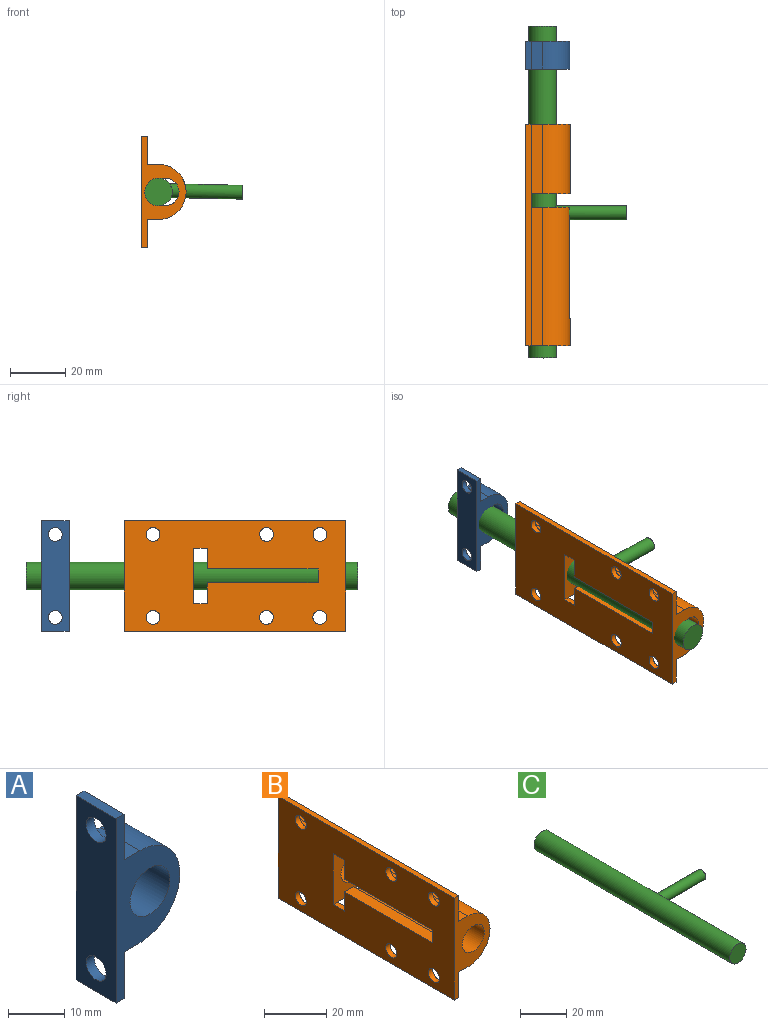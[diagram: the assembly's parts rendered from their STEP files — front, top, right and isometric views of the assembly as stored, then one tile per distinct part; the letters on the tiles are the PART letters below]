
ASSEMBLY  parts=3 mates=2
PART A: 13 faces, bbox 16x10x40 mm
  f0: plane 40x16mm, normal (0,-1,0), area 238.5mm2, adj f1,f3,f4,f5,f6,f7,f8,f9
  f1: plane 10x4mm, normal (0,0,-1), area 40mm2, adj f0,f2,f6,f9
  f2: plane 40x16mm, normal (0,1,0), area 238.5mm2, adj f1,f3,f4,f5,f6,f7,f8,f9
  f3: plane 10x4mm, normal (0,0,1), area 40mm2, adj f0,f2,f8,f9
  f4: plane 10x2mm, normal (0,0,-1), area 20mm2, adj f0,f2,f5,f6
  f5: plane 40x10mm, normal (-1,0,0), area 360.7mm2, adj f0,f2,f4,f7,f11,f12
  f6: plane 10.06x10mm, normal (1,0,0), area 81mm2, adj f0,f1,f2,f4,f12
  f7: plane 10x2mm, normal (0,0,1), area 20mm2, adj f0,f2,f5,f8
  f8: plane 10x9.94mm, normal (1,0,0), area 79.7mm2, adj f0,f2,f3,f7,f11
  f9: cylinder r=10mm len=20mm, axis (0,1,0), area 314.2mm2, adj f0,f1,f2,f3
  f10: cylinder r=5mm len=10mm, axis (0,1,0), area 314.2mm2, adj f0,f2
  f11: cylinder r=2.5mm len=5mm, axis (1,0,0), area 31.4mm2, adj f5,f8
  f12: cylinder r=2.5mm len=5mm, axis (1,0,0), area 31.4mm2, adj f5,f6
PART B: 32 faces, bbox 16.1x80x40 mm
  f0: plane 5x2mm, normal (0,0,1), area 10mm2, adj f2,f12,f13,f19
  f1: plane 5x2mm, normal (0,0,-1), area 10mm2, adj f12,f15,f18,f19
  f2: plane 15.78x7.5mm, normal (0,1,0), area 84.2mm2, adj f0,f3,f12,f16,f17,f22,f24
  f3: plane 50x4.1mm, normal (0,0,-1), area 205mm2, adj f2,f7,f13,f16
  f4: plane 50x4.1mm, normal (0,0,1), area 205mm2, adj f7,f15,f16,f18
  f5: cylinder r=10mm len=25mm, axis (0,-1,0), area 785.4mm2, adj f8,f9,f10,f19
  f6: cylinder r=5mm len=25mm, axis (0,-1,0), area 785.4mm2, adj f9,f19
  f7: plane 40x16.1mm, normal (0,-1,0), area 240.5mm2, adj f3,f4,f11,f12,f13,f14,f15,f16
  f8: plane 25x4.1mm, normal (0,0,-1), area 102.5mm2, adj f5,f9,f13,f19
  f9: plane 40x16.1mm, normal (0,1,0), area 240.5mm2, adj f5,f6,f8,f10,f11,f12,f13,f14
  f10: plane 25x4.1mm, normal (0,0,1), area 102.5mm2, adj f5,f9,f15,f19
  f11: plane 80x2mm, normal (0,0,-1), area 160mm2, adj f7,f9,f12,f13
  f12: plane 80x40mm, normal (-1,0,0), area 2782.2mm2, adj f0,f1,f2,f7,f9,f11,f14,f18
  f13: plane 80x10mm, normal (1,0,0), area 741.1mm2, adj f0,f3,f7,f8,f9,f11,f29,f30
  f14: plane 80x2mm, normal (0,0,1), area 160mm2, adj f7,f9,f12,f15
  f15: plane 80x10mm, normal (1,0,0), area 741.1mm2, adj f1,f4,f7,f9,f10,f14,f26,f27
  f16: cylinder r=10mm len=50mm, axis (0,-1,0), area 1368.7mm2, adj f2,f3,f4,f7,f18,f23,f24,f25
  f17: cylinder r=5mm len=50mm, axis (0,-1,0), area 1151.9mm2, adj f2,f7,f18,f20,f21,f22,f23,f24
  f18: plane 15.78x7.5mm, normal (0,1,0), area 84.2mm2, adj f1,f4,f12,f16,f17,f20,f25
  f19: plane 20x16.1mm, normal (0,-1,0), area 200.5mm2, adj f0,f1,f5,f6,f8,f10,f12
  f20: plane 40x4.22mm, normal (0,0,-1), area 168.8mm2, adj f12,f17,f18,f21
  f21: plane 5x4.22mm, normal (0,1,0), area 18.8mm2, adj f12,f17,f20,f22
  f22: plane 40x4.22mm, normal (0,0,1), area 168.8mm2, adj f2,f12,f17,f21
  f23: plane 5x3.22mm, normal (0,1,0), area 13.3mm2, adj f16,f17,f24,f25
  f24: plane 40x2.9mm, normal (0,0,1), area 116.1mm2, adj f2,f16,f17,f23
  f25: plane 40x2.9mm, normal (0,0,-1), area 116.1mm2, adj f16,f17,f18,f23
  f26: cylinder r=2.5mm len=5mm, axis (1,0,0), area 31.4mm2, adj f12,f15
  f27: cylinder r=2.5mm len=5mm, axis (1,0,0), area 31.4mm2, adj f12,f15
  f28: cylinder r=2.5mm len=5mm, axis (1,0,0), area 31.4mm2, adj f12,f15
  f29: cylinder r=2.5mm len=5mm, axis (1,0,0), area 31.4mm2, adj f12,f13
  f30: cylinder r=2.5mm len=5mm, axis (1,0,0), area 31.4mm2, adj f12,f13
  f31: cylinder r=2.5mm len=5mm, axis (1,0,0), area 31.4mm2, adj f12,f13
PART C: 5 faces, bbox 35.3x120x10 mm
  f0: cylinder r=2.5mm len=26.32mm, axis (-1,0,0), area 403.1mm2, adj f1,f2
  f1: plane 5x5mm, normal (1,0,0), area 19.6mm2, adj f0
  f2: cylinder r=5mm len=120mm, axis (0,1,0), area 3749.5mm2, adj f0,f3,f4
  f3: plane 10x10mm, normal (0,-1,0), area 78.5mm2, adj f2
  f4: plane 10x10mm, normal (0,1,0), area 78.5mm2, adj f2
PLACE A t=(-77.32,9.12,59.51)mm
PLACE B t=(-77.37,0.64,59.57)mm
PLACE C rot(axis=(0,1,0),1.2deg) t=(-71.75,-3.79,104.92)mm
MATE fastened B.f6 <-> A.f10  axis (0,-1,0) through (-69.82,80.64,79.57)mm
MATE cylindrical C.f2 <-> B.f5  axis (0,1,0) through (-72.27,116.21,79.57)mm
